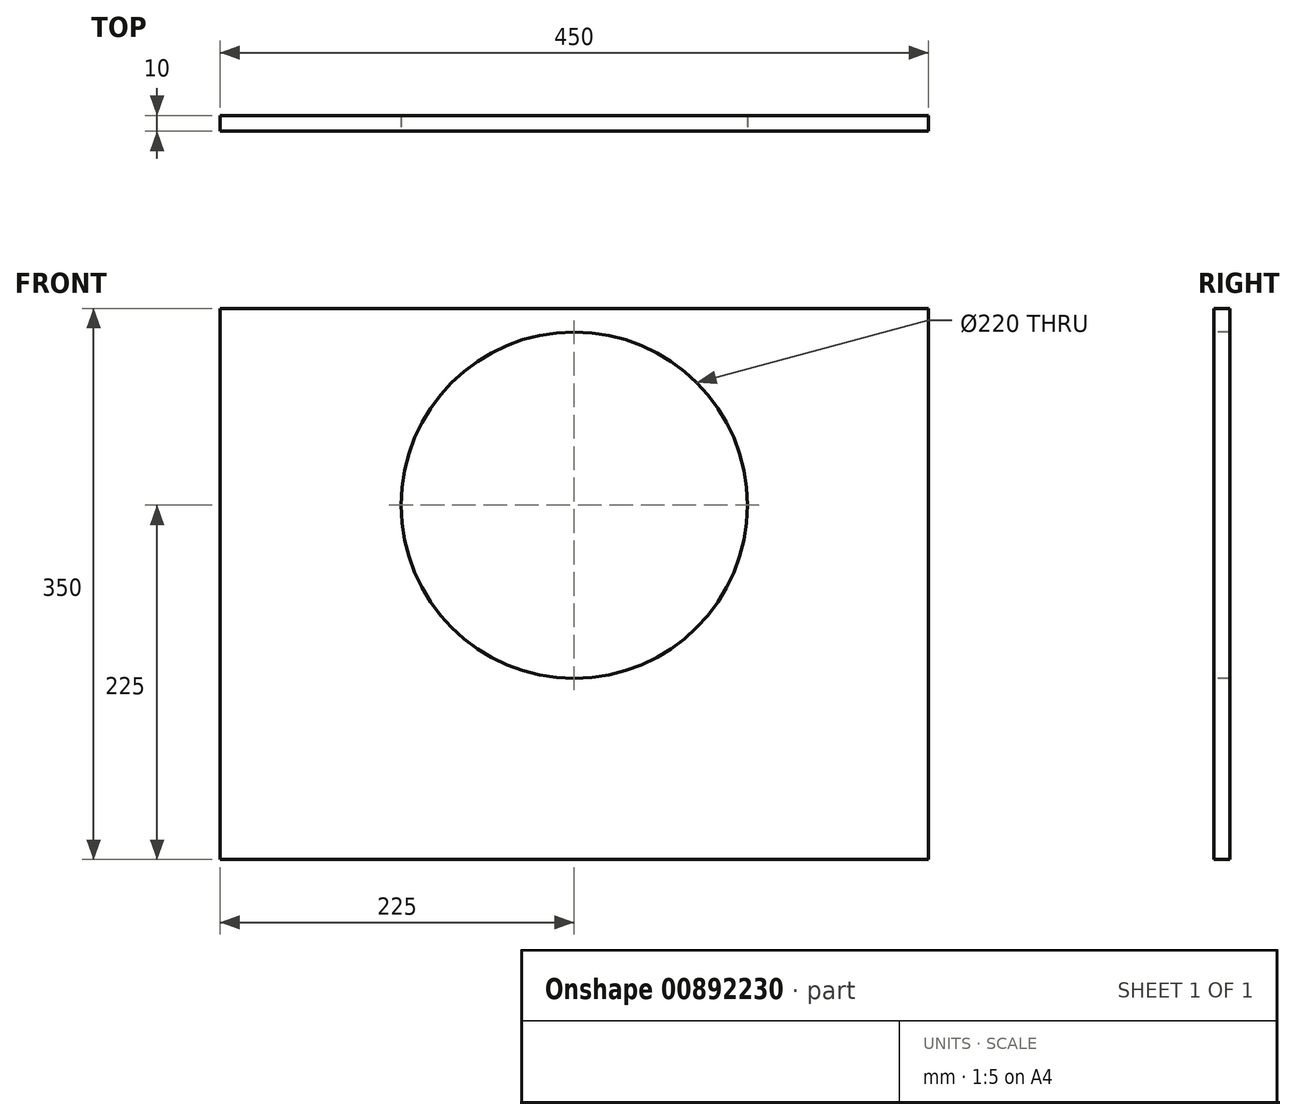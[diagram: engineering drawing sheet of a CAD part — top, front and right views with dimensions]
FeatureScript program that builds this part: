
annotation { "Feature Type Name" : "Feature", "Feature Type Description" : "" }
export const myFeature = defineFeature(function(context is Context, id is Id, definition is map)
    precondition{}
    {
        {
            var Q0;
            Q0=qCreatedBy(makeId("Front.planeOp"),FACE);
            var sketch = newSketch(context, id + "F0", { "sketchPlane" : qUnion([Q0])});
            skLineSegment(sketch, "E0.bottom", {"start": v(0, 0) * mm, "end": v(450, 0) * mm});
            skLineSegment(sketch, "E0.top", {"start": v(0, 350) * mm, "end": v(450, 350) * mm});
            skLineSegment(sketch, "E0.left", {"start": v(0, 0) * mm, "end": v(0, 350) * mm});
            skLineSegment(sketch, "E0.right", {"start": v(450, 0) * mm, "end": v(450, 350) * mm});
            skCircle(sketch, "E1", {"center": v(225, 225) * mm, "radius": 110 * mm});
            skPoint(sketch, "E1.centerSnap0", {"position": v(225, 350) * mm});
            skSolve(sketch);
        }
        {
            var Q0;
            Q0 = qSketchRegion(id + "F0", true);
            extrude(context, id + "F1", {"entities" : qUnion([Q0]), "oppositeDirection" : true, "depth" : 10 * mm, "offsetDistance" : 25 * mm});
        }
    });
